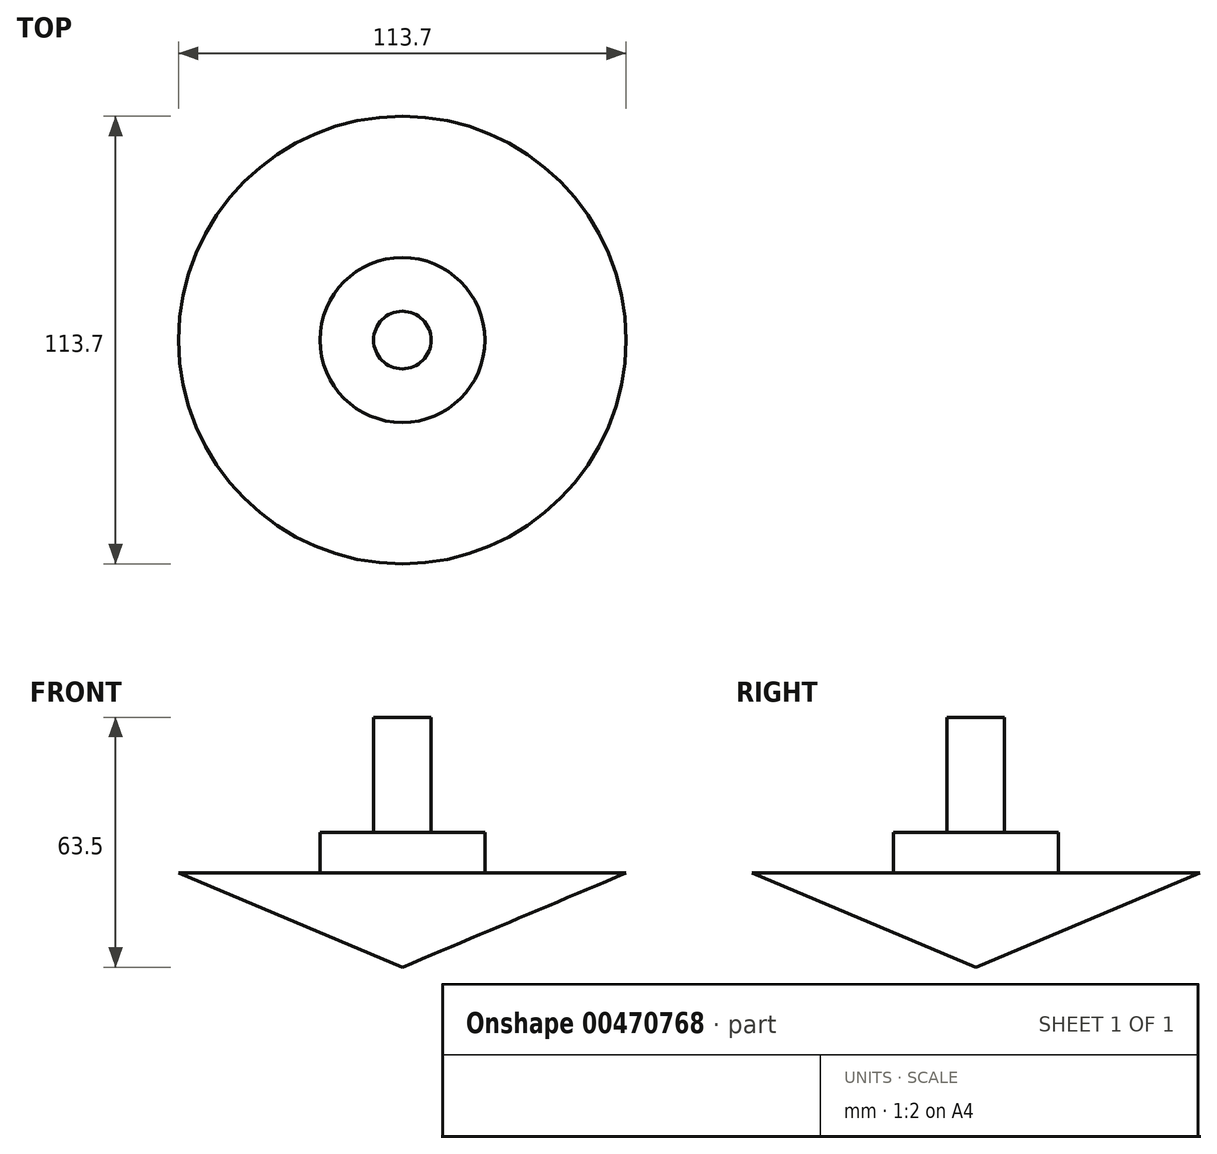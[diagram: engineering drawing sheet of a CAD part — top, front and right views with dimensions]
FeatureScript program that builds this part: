
annotation { "Feature Type Name" : "Feature", "Feature Type Description" : "" }
export const myFeature = defineFeature(function(context is Context, id is Id, definition is map)
    precondition{}
    {
        {
            var Q0;
            Q0=qCreatedBy(makeId("Front.planeOp"),FACE);
            var sketch = newSketch(context, id + "F0", { "sketchPlane" : qUnion([Q0])});
            skLineSegment(sketch, "E0", {"start": v(0, 0) * mm, "end": v(56.85, 23.94) * mm});
            skLineSegment(sketch, "E1", {"start": v(56.85, 23.94) * mm, "end": v(20.95, 23.94) * mm});
            skLineSegment(sketch, "E2", {"start": v(20.95, 34.24) * mm, "end": v(20.95, 23.94) * mm});
            skLineSegment(sketch, "E3", {"start": v(20.95, 34.24) * mm, "end": v(7.31, 34.24) * mm});
            skLineSegment(sketch, "E4", {"start": v(7.31, 34.24) * mm, "end": v(7.31, 63.5) * mm});
            skLineSegment(sketch, "E5", {"start": v(7.31, 63.5) * mm, "end": v(0, 63.5) * mm});
            skLineSegment(sketch, "E6", {"start": v(7.31, 34.24) * mm, "end": v(0, 34.24) * mm});
            skLineSegment(sketch, "E7", {"start": v(0, 34.24) * mm, "end": v(0, 23.94) * mm});
            skLineSegment(sketch, "E8", {"start": v(0, 23.94) * mm, "end": v(20.95, 23.94) * mm});
            skLineSegment(sketch, "E9", {"start": v(0, 0) * mm, "end": v(0, 63.5) * mm});
            skSolve(sketch);
        }
        {
            var Q0;
            Q0 = qSketchRegion(id + "F0", true);
            var Q1;
            Q1=sQuery(id+"F0.wireOp",EDGE,"E9");
            revolve(context, id + "F1", {"entities" : qUnion([Q0]), "axis" : qUnion([Q1]), "revolveType" : RevolveType.FULL});
        }
    });
